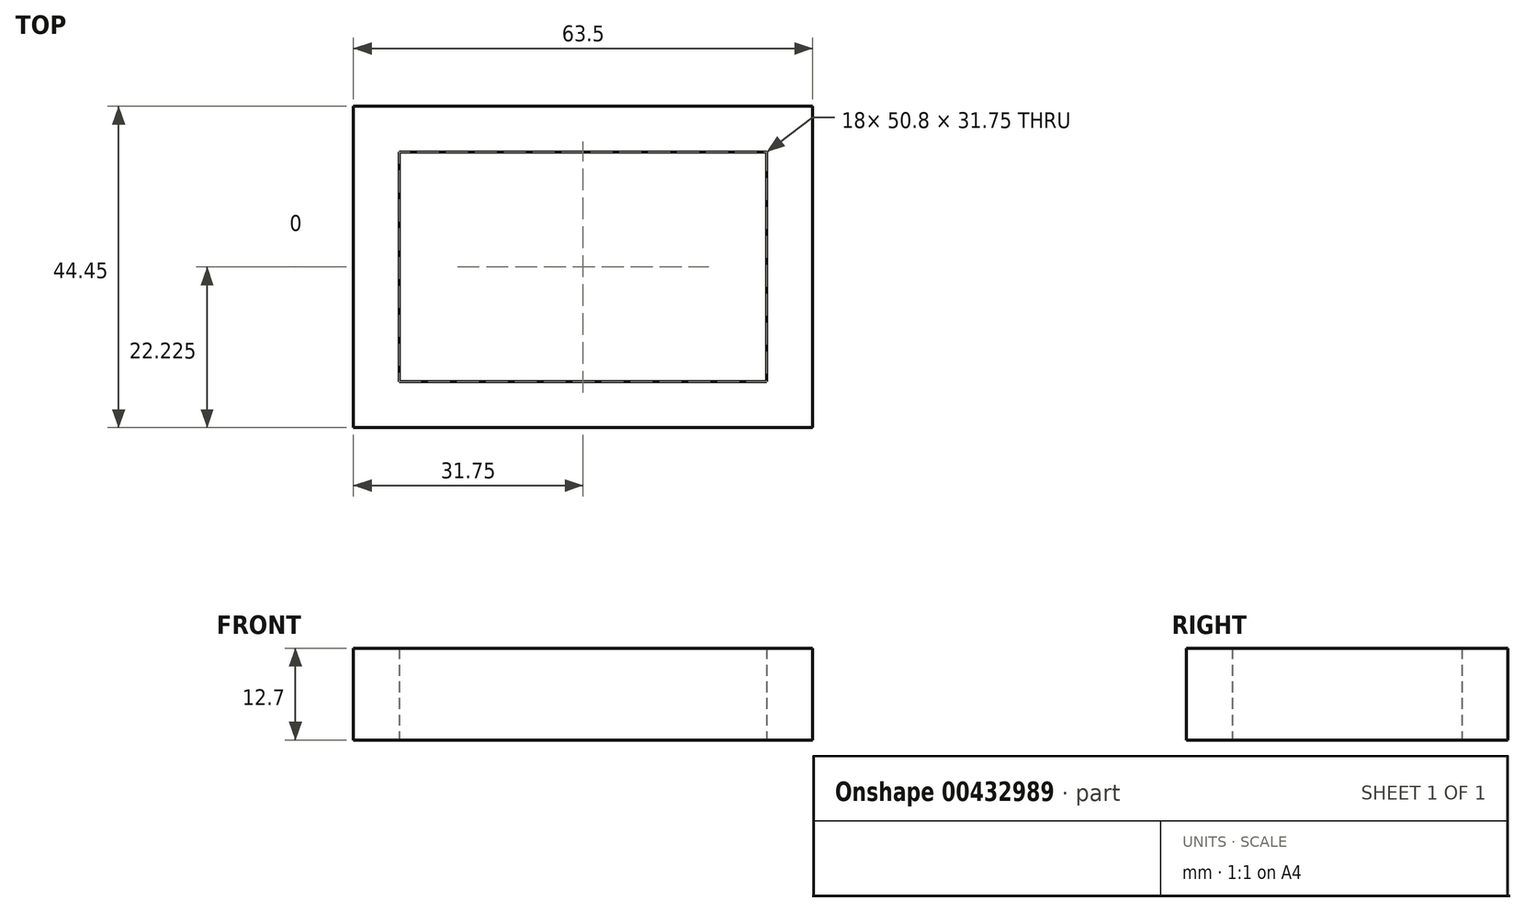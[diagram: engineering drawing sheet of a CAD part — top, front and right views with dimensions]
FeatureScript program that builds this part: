
annotation { "Feature Type Name" : "Feature", "Feature Type Description" : "" }
export const myFeature = defineFeature(function(context is Context, id is Id, definition is map)
    precondition{}
    {
        {
            var Q0;
            Q0=qCreatedBy(makeId("Top.planeOp"),FACE);
            var sketch = newSketch(context, id + "F0", { "sketchPlane" : qUnion([Q0])});
            skLineSegment(sketch, "E0.bottom", {"start": v(0, 0) * mm, "end": v(50.8, 0) * mm});
            skLineSegment(sketch, "E0.top", {"start": v(0, 31.75) * mm, "end": v(50.8, 31.75) * mm});
            skLineSegment(sketch, "E0.left", {"start": v(0, 0) * mm, "end": v(0, 31.75) * mm});
            skLineSegment(sketch, "E0.right", {"start": v(50.8, 0) * mm, "end": v(50.8, 31.75) * mm});
            skLineSegment(sketch, "E1.0", {"start": v(57.15, -6.35) * mm, "end": v(57.15, 38.1) * mm});
            skLineSegment(sketch, "E1.1", {"start": v(-6.35, -6.35) * mm, "end": v(57.15, -6.35) * mm});
            skLineSegment(sketch, "E1.2", {"start": v(-6.35, -6.35) * mm, "end": v(-6.35, 38.1) * mm});
            skLineSegment(sketch, "E1.3", {"start": v(-6.35, 38.1) * mm, "end": v(57.15, 38.1) * mm});
            skSolve(sketch);
        }
        {
            var Q0;
            Q0 = qSketchRegion(id + "F0", true);
            extrude(context, id + "F1", {"entities" : qUnion([Q0]), "depth" : 12.7 * mm});
        }
    });
